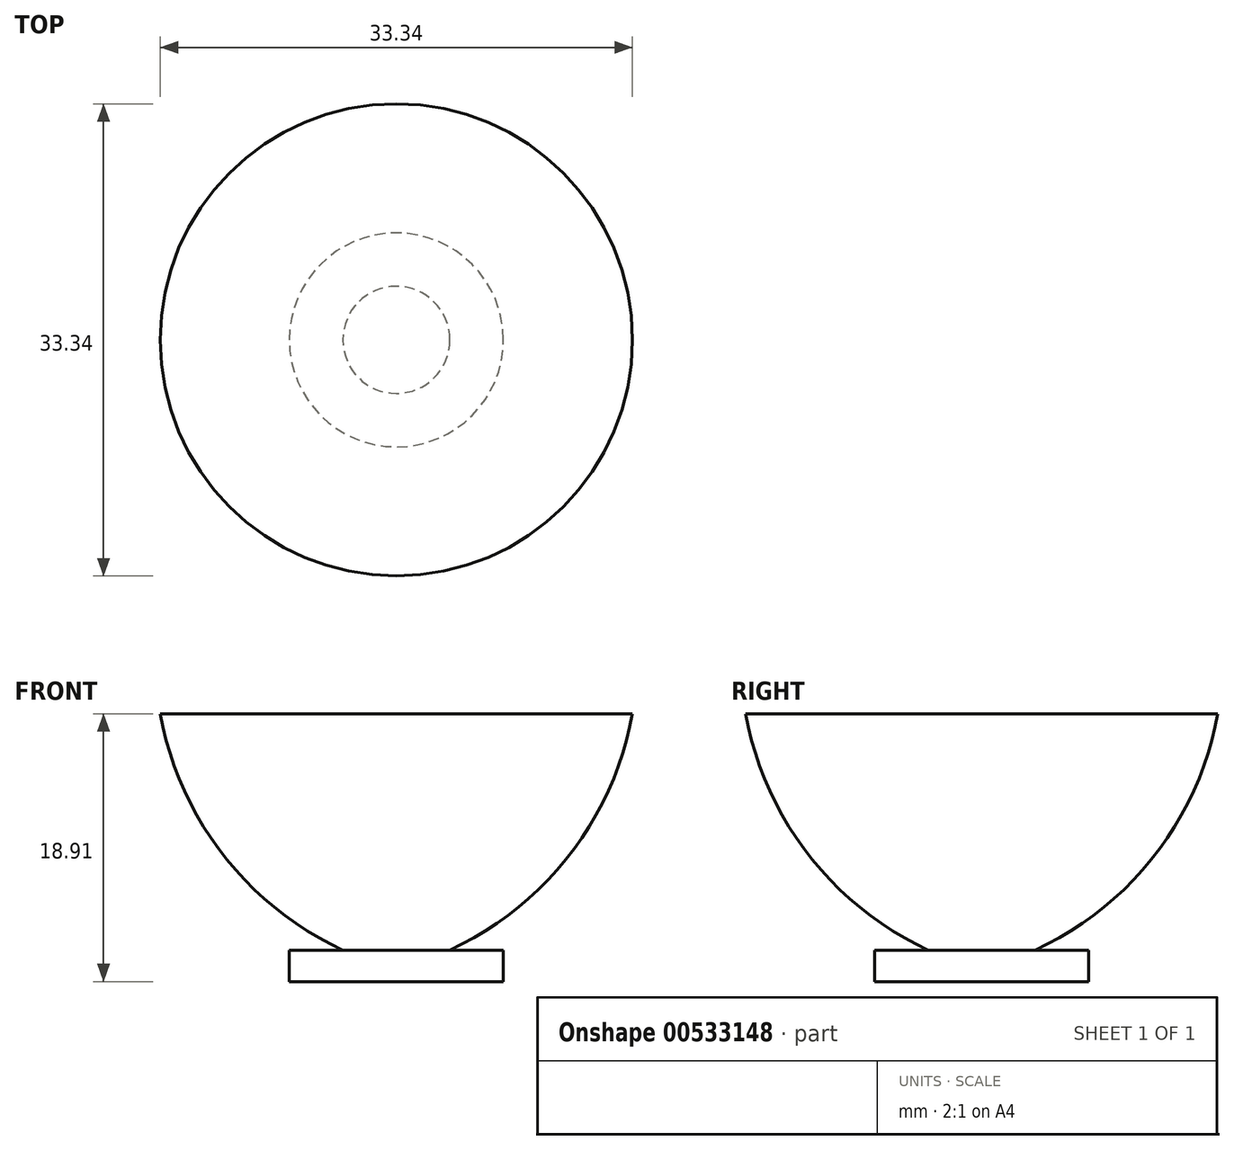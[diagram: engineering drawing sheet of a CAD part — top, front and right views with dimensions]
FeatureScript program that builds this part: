
annotation { "Feature Type Name" : "Feature", "Feature Type Description" : "" }
export const myFeature = defineFeature(function(context is Context, id is Id, definition is map)
    precondition{}
    {
        {
            var Q0;
            Q0=qCreatedBy(makeId("Front.planeOp"),FACE);
            var sketch = newSketch(context, id + "F0", { "sketchPlane" : qUnion([Q0])});
            skLineSegment(sketch, "E0.bottom", {"start": v(0, 0) * mm, "end": v(-16.67, 0) * mm});
            skLineSegment(sketch, "E0.left", {"start": v(0, 0) * mm, "end": v(0, -16.68) * mm});
            skLineSegment(sketch, "E1.bottom", {"start": v(0, -16.68) * mm, "end": v(-7.56, -16.68) * mm});
            skLineSegment(sketch, "E1.top", {"start": v(0, -18.9) * mm, "end": v(-7.56, -18.9) * mm});
            skLineSegment(sketch, "E1.left", {"start": v(0, -16.68) * mm, "end": v(0, -18.9) * mm});
            skLineSegment(sketch, "E1.right", {"start": v(-7.56, -16.68) * mm, "end": v(-7.56, -18.9) * mm});
            skArc(sketch, "E2", {"start": v(-16.67, 0) * mm, "mid": v(-12.27, -9.92) * mm, "end": v(-3.78, -16.68) * mm});
            skSolve(sketch);
        }
        {
            var Q0;
            Q0 = qSketchRegion(id + "F0", true);
            var Q1;
            Q1=sQuery(id+"F0.wireOp",EDGE,"E0.left");
            revolve(context, id + "F1", {"entities" : qUnion([Q0]), "axis" : qUnion([Q1]), "revolveType" : RevolveType.FULL});
        }
    });
